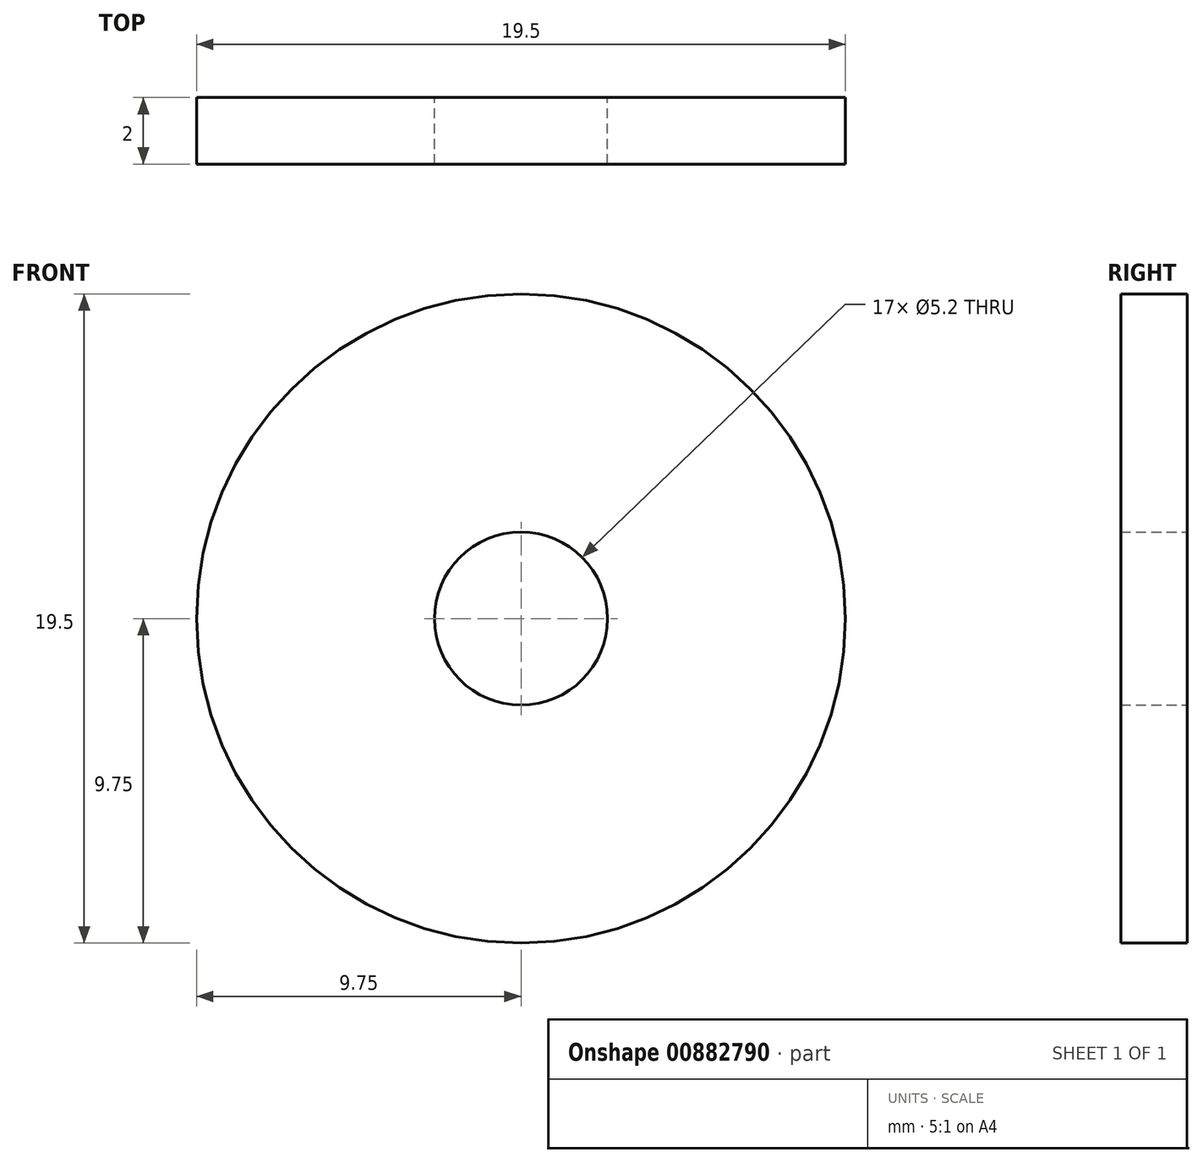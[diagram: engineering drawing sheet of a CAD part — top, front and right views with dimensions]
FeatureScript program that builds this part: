
annotation { "Feature Type Name" : "Feature", "Feature Type Description" : "" }
export const myFeature = defineFeature(function(context is Context, id is Id, definition is map)
    precondition{}
    {
        {
            var Q0;
            Q0=qCreatedBy(makeId("Front.planeOp"),FACE);
            var sketch = newSketch(context, id + "F0", { "sketchPlane" : qUnion([Q0])});
            skCircle(sketch, "E0", {"center": v(0, 0) * mm, "radius": 9.75 * mm});
            skCircle(sketch, "E1", {"center": v(0, 0) * mm, "radius": 2.6 * mm});
            skSolve(sketch);
        }
        {
            var Q0;
            Q0 = qSketchRegion(id + "F0", true);
            extrude(context, id + "F1", {"entities" : qUnion([Q0]), "depth" : 2 * mm, "offsetDistance" : 25.4 * mm});
        }
    });
